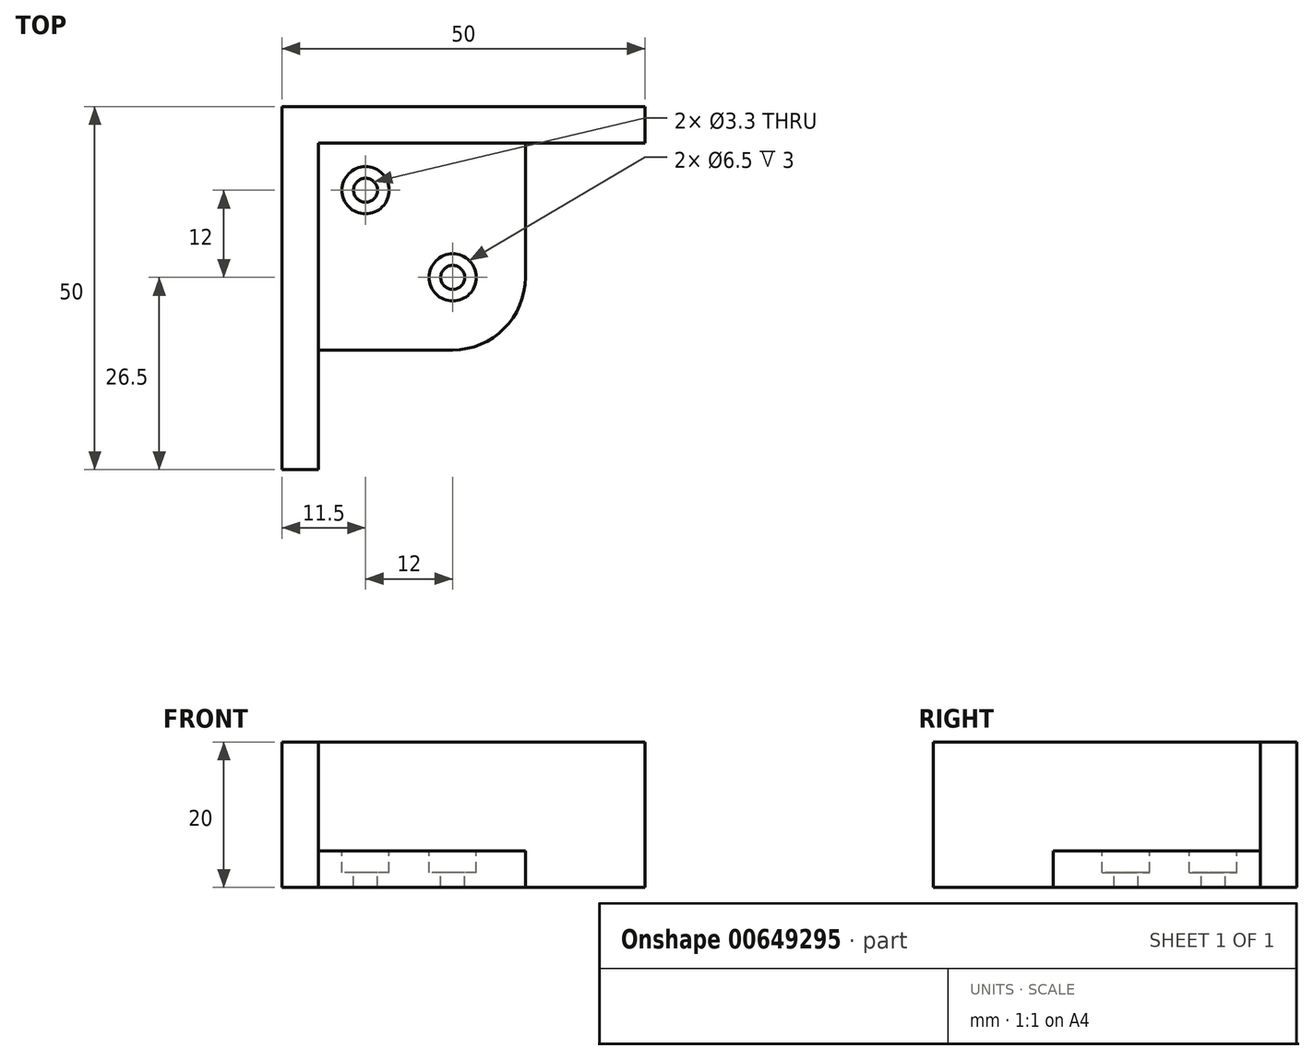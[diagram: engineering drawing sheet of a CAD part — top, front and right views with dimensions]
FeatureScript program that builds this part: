
annotation { "Feature Type Name" : "Feature", "Feature Type Description" : "" }
export const myFeature = defineFeature(function(context is Context, id is Id, definition is map)
    precondition{}
    {
        {
            var Q0;
            Q0=qCreatedBy(makeId("Top.planeOp"),FACE);
            var sketch = newSketch(context, id + "F0", { "sketchPlane" : qUnion([Q0])});
            skLineSegment(sketch, "E0.bottom", {"start": v(-220, 10) * mm, "end": v(220, 10) * mm, "construction": true});
            skLineSegment(sketch, "E0.top", {"start": v(-220, -10) * mm, "end": v(220, -10) * mm, "construction": true});
            skLineSegment(sketch, "E0.left", {"start": v(-220, 10) * mm, "end": v(-220, -10) * mm, "construction": true});
            skLineSegment(sketch, "E0.right", {"start": v(220, 10) * mm, "end": v(220, -10) * mm, "construction": true});
            skLineSegment(sketch, "E1.bottom", {"start": v(-263.5, 226) * mm, "end": v(-243.5, 226) * mm, "construction": true});
            skLineSegment(sketch, "E1.top", {"start": v(-263.5, -226) * mm, "end": v(-243.5, -226) * mm, "construction": true});
            skLineSegment(sketch, "E1.left", {"start": v(-263.5, 226) * mm, "end": v(-263.5, -226) * mm, "construction": true});
            skLineSegment(sketch, "E1.right", {"start": v(-243.5, 226) * mm, "end": v(-243.5, -226) * mm, "construction": true});
            skLineSegment(sketch, "E2.MirrorCS", {"start": v(243.5, 226) * mm, "end": v(243.5, -226) * mm, "construction": true});
            skLineSegment(sketch, "E3.MirrorCS", {"start": v(263.5, 226) * mm, "end": v(243.5, 226) * mm, "construction": true});
            skLineSegment(sketch, "E4.MirrorCS", {"start": v(263.5, 226) * mm, "end": v(263.5, -226) * mm, "construction": true});
            skLineSegment(sketch, "E5.MirrorCS", {"start": v(263.5, -226) * mm, "end": v(243.5, -226) * mm, "construction": true});
            skCircle(sketch, "E6", {"center": v(-220, 23) * mm, "radius": 8 * mm, "construction": true});
            skCircle(sketch, "E7.MirrorC", {"center": v(220, 23) * mm, "radius": 8 * mm, "construction": true});
            skCircle(sketch, "E8.MirrorC", {"center": v(-220, -23) * mm, "radius": 8 * mm, "construction": true});
            skCircle(sketch, "E9.MirrorC", {"center": v(220, -23) * mm, "radius": 8 * mm, "construction": true});
            skCircle(sketch, "E10", {"center": v(-220, 23) * mm, "radius": 6 * mm, "construction": true});
            skCircle(sketch, "E11.MirrorC", {"center": v(-220, -23) * mm, "radius": 6 * mm, "construction": true});
            skCircle(sketch, "E12.MirrorC", {"center": v(220, -23) * mm, "radius": 6 * mm, "construction": true});
            skCircle(sketch, "E13.MirrorC", {"center": v(220, 23) * mm, "radius": 6 * mm, "construction": true});
            skCircle(sketch, "E14", {"center": v(-232, -226) * mm, "radius": 6 * mm, "construction": true});
            skCircle(sketch, "E15", {"center": v(-232, -226) * mm, "radius": 8 * mm, "construction": true});
            skLineSegment(sketch, "E16", {"start": v(-226, -23) * mm, "end": v(-226, -226) * mm});
            skLineSegment(sketch, "E17", {"start": v(-238, -226) * mm, "end": v(-238, 226) * mm});
            skCircle(sketch, "E18.MirrorC", {"center": v(-232, 226) * mm, "radius": 8 * mm, "construction": true});
            skCircle(sketch, "E19.MirrorC", {"center": v(-232, 226) * mm, "radius": 6 * mm, "construction": true});
            skCircle(sketch, "E20.MirrorC", {"center": v(232, -226) * mm, "radius": 6 * mm, "construction": true});
            skCircle(sketch, "E21.MirrorC", {"center": v(232, -226) * mm, "radius": 8 * mm, "construction": true});
            skCircle(sketch, "E22.MirrorC", {"center": v(232, 226) * mm, "radius": 6 * mm, "construction": true});
            skCircle(sketch, "E23.MirrorC", {"center": v(232, 226) * mm, "radius": 8 * mm, "construction": true});
            skLineSegment(sketch, "E24", {"start": v(-220, -17) * mm, "end": v(0, -17) * mm});
            skPoint(sketch, "E24.startSnap0", {"position": v(-220, 0) * mm});
            skLineSegment(sketch, "E25", {"start": v(0, -17) * mm, "end": v(220, -17) * mm});
            skLineSegment(sketch, "E26", {"start": v(226, -23) * mm, "end": v(226, -226) * mm});
            skLineSegment(sketch, "E27", {"start": v(238, -226) * mm, "end": v(238, 226) * mm});
            skCircle(sketch, "E28", {"center": v(-220, 214) * mm, "radius": 6 * mm, "construction": true});
            skCircle(sketch, "E29", {"center": v(-220, 214) * mm, "radius": 8 * mm, "construction": true});
            skLineSegment(sketch, "E30", {"start": v(-232, 226) * mm, "end": v(-220, 214) * mm, "construction": true});
            skCircle(sketch, "E31.MirrorC", {"center": v(220, 214) * mm, "radius": 6 * mm, "construction": true});
            skCircle(sketch, "E32.MirrorC", {"center": v(220, 214) * mm, "radius": 8 * mm, "construction": true});
            skLineSegment(sketch, "E33", {"start": v(-231.84, 232) * mm, "end": v(220.16, 220) * mm});
            skLineSegment(sketch, "E34", {"start": v(226, 214) * mm, "end": v(226, 23) * mm});
            skLineSegment(sketch, "E35", {"start": v(220, 17) * mm, "end": v(0, 17) * mm});
            skLineSegment(sketch, "E36", {"start": v(0, 17) * mm, "end": v(-220, 17) * mm});
            skLineSegment(sketch, "E37", {"start": v(-226, 23) * mm, "end": v(-226, 214) * mm});
            skLineSegment(sketch, "E38", {"start": v(-220.16, 220) * mm, "end": v(231.84, 232) * mm});
            skLineSegment(sketch, "E39", {"start": v(-243.5, 214) * mm, "end": v(-263.5, 214) * mm, "construction": true});
            skArc(sketch, "E40", {"start": v(-226, 23) * mm, "mid": v(-224.24, 18.76) * mm, "end": v(-220, 17) * mm});
            skArc(sketch, "E41", {"start": v(-220, -17) * mm, "mid": v(-224.24, -18.76) * mm, "end": v(-226, -23) * mm});
            skArc(sketch, "E42", {"start": v(-238, -226) * mm, "mid": v(-232, -232) * mm, "end": v(-226, -226) * mm});
            skArc(sketch, "E43", {"start": v(226, -226) * mm, "mid": v(232, -232) * mm, "end": v(238, -226) * mm});
            skArc(sketch, "E44", {"start": v(226, -23) * mm, "mid": v(224.24, -18.76) * mm, "end": v(220, -17) * mm});
            skArc(sketch, "E45", {"start": v(220, 17) * mm, "mid": v(224.24, 18.76) * mm, "end": v(226, 23) * mm});
            skArc(sketch, "E46", {"start": v(226, 214) * mm, "mid": v(224.3, 218.19) * mm, "end": v(220.16, 220) * mm});
            skArc(sketch, "E47", {"start": v(238, 226) * mm, "mid": v(236.19, 230.3) * mm, "end": v(231.84, 232) * mm});
            skArc(sketch, "E48", {"start": v(-220.16, 220) * mm, "mid": v(-224.3, 218.19) * mm, "end": v(-226, 214) * mm});
            skArc(sketch, "E49", {"start": v(-231.84, 232) * mm, "mid": v(-236.19, 230.3) * mm, "end": v(-238, 226) * mm});
            skLineSegment(sketch, "E50.bottom", {"start": v(-267, 62.04) * mm, "end": v(-240, 62.04) * mm, "construction": true});
            skLineSegment(sketch, "E50.top", {"start": v(-267, -56.61) * mm, "end": v(-240, -56.61) * mm, "construction": true});
            skLineSegment(sketch, "E50.left", {"start": v(-267, 62.04) * mm, "end": v(-267, -56.61) * mm, "construction": true});
            skLineSegment(sketch, "E50.right", {"start": v(-240, 62.04) * mm, "end": v(-240, -56.61) * mm, "construction": true});
            skLineSegment(sketch, "E51", {"start": v(-253.5, 62.04) * mm, "end": v(-253.5, -56.61) * mm, "construction": true});
            skSolve(sketch);
        }
        {
            var Q0;
            Q0=sQuery(id+"F0.wireOp",EDGE,"E16");
            var Q1;
            Q1=sQuery(id+"F0.wireOp",EDGE,"E42");
            var Q2;
            Q2=sQuery(id+"F0.wireOp",EDGE,"E17");
            var Q3;
            Q3=sQuery(id+"F0.wireOp",EDGE,"E24");
            var Q4;
            Q4=sQuery(id+"F0.wireOp",EDGE,"E33");
            var Q5;
            Q5=sQuery(id+"F0.wireOp",EDGE,"E49");
            var Q6;
            Q6=sQuery(id+"F0.wireOp",EDGE,"E46");
            var Q7;
            Q7=sQuery(id+"F0.wireOp",EDGE,"E34");
            var Q8;
            Q8=sQuery(id+"F0.wireOp",EDGE,"E45");
            var Q9;
            Q9=sQuery(id+"F0.wireOp",EDGE,"E35");
            var Q10;
            Q10=sQuery(id+"F0.wireOp",EDGE,"E41");
            extrude(context, id + "F1", {"bodyType" : ToolBodyType.SURFACE, "surfaceEntities" : qUnion([Q0, Q1, Q2, Q3, Q4, Q5, Q6, Q7, Q8, Q9, Q10]), "depth" : 6 * mm, "offsetDistance" : 25 * mm});
        }
        {
            var Q0;
            Q0=sQuery(id+"F0.wireOp",EDGE,"E36");
            var Q1;
            Q1=sQuery(id+"F0.wireOp",EDGE,"E25");
            var Q2;
            Q2=sQuery(id+"F0.wireOp",EDGE,"E26");
            var Q3;
            Q3=sQuery(id+"F0.wireOp",EDGE,"E44");
            var Q4;
            Q4=sQuery(id+"F0.wireOp",EDGE,"E27");
            var Q5;
            Q5=sQuery(id+"F0.wireOp",EDGE,"E43");
            var Q6;
            Q6=sQuery(id+"F0.wireOp",EDGE,"E47");
            var Q7;
            Q7=sQuery(id+"F0.wireOp",EDGE,"E38");
            var Q8;
            Q8=sQuery(id+"F0.wireOp",EDGE,"E48");
            var Q9;
            Q9=sQuery(id+"F0.wireOp",EDGE,"E37");
            var Q10;
            Q10=sQuery(id+"F0.wireOp",EDGE,"E40");
            extrude(context, id + "F2", {"bodyType" : ToolBodyType.SURFACE, "surfaceEntities" : qUnion([Q0, Q1, Q2, Q3, Q4, Q5, Q6, Q7, Q8, Q9, Q10]), "depth" : 6 * mm, "offsetDistance" : 25 * mm});
        }
        {
            var Q0;
            Q0=qCreatedBy(makeId("Top.planeOp"),FACE);
            var sketch = newSketch(context, id + "F3", { "sketchPlane" : qUnion([Q0])});
            skLineSegment(sketch, "E52.bottom", {"start": v(-266.67, 257.5) * mm, "end": v(-83.38, 257.5) * mm});
            skLineSegment(sketch, "E52.top", {"start": v(-266.67, 237.5) * mm, "end": v(-83.38, 237.5) * mm});
            skLineSegment(sketch, "E52.left", {"start": v(-266.67, 257.5) * mm, "end": v(-266.67, 237.5) * mm});
            skLineSegment(sketch, "E52.right", {"start": v(-83.38, 257.5) * mm, "end": v(-83.38, 237.5) * mm});
            skLineSegment(sketch, "E53.bottom", {"start": v(-243.5, 237.5) * mm, "end": v(-263.5, 237.5) * mm});
            skLineSegment(sketch, "E53.top", {"start": v(-243.5, 173.56) * mm, "end": v(-263.5, 173.56) * mm});
            skLineSegment(sketch, "E53.left", {"start": v(-243.5, 237.5) * mm, "end": v(-243.5, 173.56) * mm});
            skLineSegment(sketch, "E53.right", {"start": v(-263.5, 237.5) * mm, "end": v(-263.5, 173.56) * mm});
            skCircle(sketch, "E54", {"center": v(-220, 214) * mm, "radius": 10 * mm});
            skLineSegment(sketch, "E55", {"start": v(-243.5, 187.5) * mm, "end": v(-238.5, 187.5) * mm});
            skLineSegment(sketch, "E56", {"start": v(-238.5, 187.5) * mm, "end": v(-238.5, 232.5) * mm});
            skLineSegment(sketch, "E57", {"start": v(-238.5, 232.5) * mm, "end": v(-193.5, 232.5) * mm});
            skLineSegment(sketch, "E58", {"start": v(-193.5, 232.5) * mm, "end": v(-193.5, 237.5) * mm});
            skLineSegment(sketch, "E59", {"start": v(-220, 204) * mm, "end": v(-238.5, 204) * mm});
            skLineSegment(sketch, "E60", {"start": v(-210, 214) * mm, "end": v(-210, 232.5) * mm});
            skSolve(sketch);
        }
        {
            var Q0;
            {var subQ1=sQuery(id+"F3.wireOp",EDGE,"E55");Q0=makeQuery(id+"F3.imprint","IMPRINT",FACE,{"disambiguationData":[TD([[makeQuery(id+"F3.imprint","IMPRINT",EDGE,{"derivedFrom":subQ1}),1.0]])]});}
            var Q1;
            {var subQ0=sQuery(id+"F3.wireOp",EDGE,"E59");Q1=makeQuery(id+"F3.imprint","IMPRINT",FACE,{"disambiguationData":[TD([[makeQuery(id+"F3.imprint","IMPRINT",EDGE,{"derivedFrom":subQ0}),-1.0]])]});}
            var Q2;
            {var subQ0=sQuery(id+"F3.wireOp",EDGE,"E54");var subQ1=makeQuery(id+"F3.imprint","INTERSECT",VERTEX,{"derivedFrom":[subQ0,sQuery(id+"F3.wireOp",EDGE,"E59")]});Q2=makeQuery(id+"F3.imprint","IMPRINT",FACE,{"disambiguationData":[TD([[makeQuery(id+"F3.imprint","IMPRINT",EDGE,{"disambiguationData":[TD([[subQ1,1.0]])],"derivedFrom":subQ0}),1.0]])]});}
            extrude(context, id + "F4", {"entities" : qUnion([Q0, Q1, Q2]), "depth" : 5 * mm, "offsetDistance" : 25 * mm});
        }
        {
            var Q0;
            {var subQ1=sQuery(id+"F3.wireOp",EDGE,"E55");Q0=makeQuery(id+"F3.imprint","IMPRINT",FACE,{"disambiguationData":[TD([[makeQuery(id+"F3.imprint","IMPRINT",EDGE,{"derivedFrom":subQ1}),1.0]])]});}
            extrude(context, id + "F5", {"entities" : qUnion([Q0]), "operationType" : NewBodyOperationType.ADD, "depth" : 20 * mm, "offsetDistance" : 25 * mm});
        }
        {
            var Q0;
            Q0=makeQuery(id+"F4.opExtrude","CAP_FACE",FACE,{"disambiguationData":[OSD([sQuery(id+"F3.wireOp",EDGE,"E52.top"),sQuery(id+"F3.wireOp",EDGE,"E53.left"),sQuery(id+"F3.wireOp",EDGE,"E54"),sQuery(id+"F3.wireOp",EDGE,"E55"),sQuery(id+"F3.wireOp",EDGE,"E56"),sQuery(id+"F3.wireOp",EDGE,"E57"),sQuery(id+"F3.wireOp",EDGE,"E58"),sQuery(id+"F3.wireOp",EDGE,"E59"),sQuery(id+"F3.wireOp",EDGE,"E60")])],"isStart":false});
            var sketch = newSketch(context, id + "F6", { "sketchPlane" : qUnion([Q0])});
            skPoint(sketch, "E61", {"position": v(-232, 226) * mm});
            skPoint(sketch, "E62", {"position": v(-220, 214) * mm});
            skSolve(sketch);
        }
        {
            var Q0;
            Q0=sQuery(id+"F6.wireOp",VERTEX,"E61");
            var Q1;
            Q1=sQuery(id+"F6.wireOp",VERTEX,"E62");
            var Q2;
            Q2=makeQuery(id+"F4.opExtrude","SWEPT_BODY",BODY,{"disambiguationData":[OSD([sQuery(id+"F3.wireOp",EDGE,"E52.top"),sQuery(id+"F3.wireOp",EDGE,"E53.left"),sQuery(id+"F3.wireOp",EDGE,"E54"),sQuery(id+"F3.wireOp",EDGE,"E55"),sQuery(id+"F3.wireOp",EDGE,"E56"),sQuery(id+"F3.wireOp",EDGE,"E57"),sQuery(id+"F3.wireOp",EDGE,"E58"),sQuery(id+"F3.wireOp",EDGE,"E59"),sQuery(id+"F3.wireOp",EDGE,"E60")])]});
            hole(context, id + "F7", {"style" : HoleStyle.C_BORE, "endStyle" : HoleEndStyle.THROUGH, "standardTappedOrClearance" : lookupTablePath({ "standard" : "ISO", "fit" : "Normal", "size" : "M3", "type" : "Clearance" }), "standardBlindInLast" : lookupTablePath({ "fit" : "Standard", "standard" : "ISO", "size" : "M3", "type" : "Clearance" }), "holeDiameter" : 3.3 * mm, "cBoreDiameter" : 6.5 * mm, "cBoreDepth" : 3 * mm, "majorDiameter" : 5 * mm, "isTappedThrough" : true, "tappedDepth" : 15 * mm, "tapClearance" : 0, "startFromSketch" : true, "locations" : qUnion([Q0, Q1]), "scope" : qUnion([Q2])});
        }
    });
